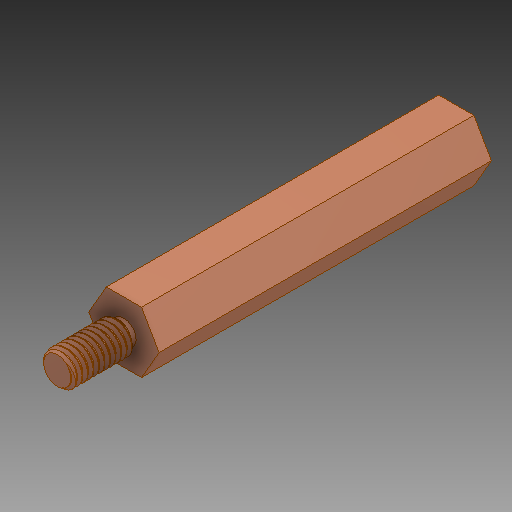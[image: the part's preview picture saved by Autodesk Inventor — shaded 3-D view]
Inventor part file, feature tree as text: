
AUTODESK INVENTOR PART (.ipt)
format: ipt  version: 2020 (Build 240168000, 168)  size: 2,289,152 bytes
history: native  units: mm
features: other x1, extrude x1, sketch x1, projected_geometry x1, imported_body x1
ambient origin geometry x8: Origin, YZ Plane, XZ Plane, XY Plane, X Axis, Y Axis, Z Axis, Center Point
bodies: Body1 (feature_tree)
feature tree (5):
  other  "Твердое тело1"
  extrude  "Выдавливание1"  Depth=5.0mm TaperAngle=0.0deg
  sketch  "Эскиз1"
  projected_geometry  "Спроецированная петля1"
  imported_body  "БазТело1"
